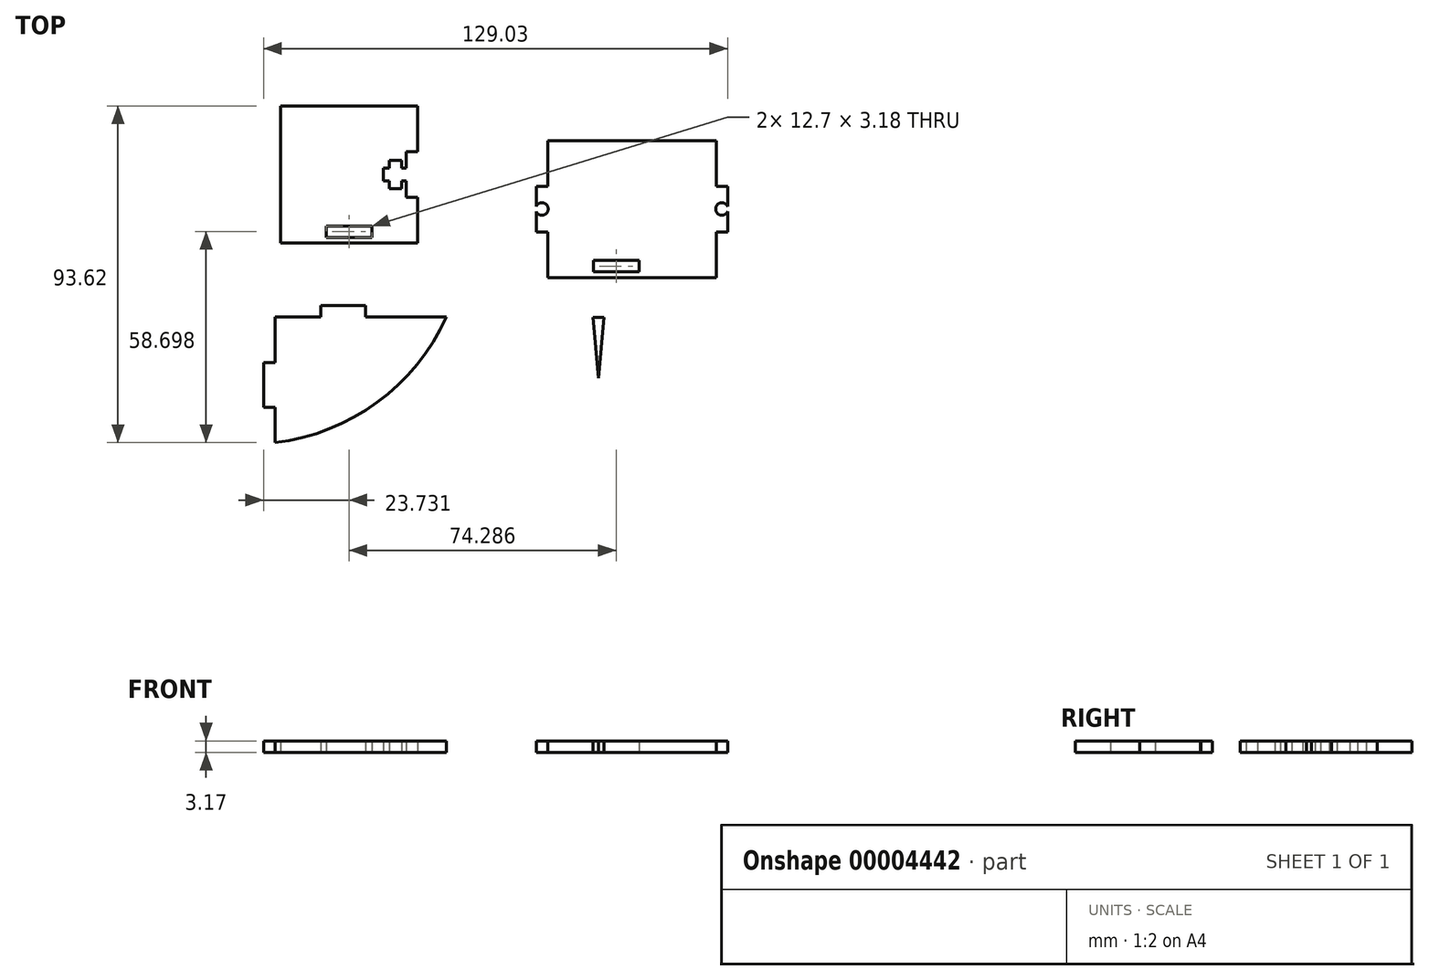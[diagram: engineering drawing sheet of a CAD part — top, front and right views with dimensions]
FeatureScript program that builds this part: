
annotation { "Feature Type Name" : "Feature", "Feature Type Description" : "" }
export const myFeature = defineFeature(function(context is Context, id is Id, definition is map)
    precondition{}
    {
        {
            var Q0;
            Q0=qCreatedBy(makeId("Top.planeOp"),FACE);
            var sketch = newSketch(context, id + "F0", { "sketchPlane" : qUnion([Q0])});
            skLineSegment(sketch, "E0.bottom", {"start": v(-61.4, 49.08) * mm, "end": v(-23.3, 49.08) * mm});
            skLineSegment(sketch, "E0.top", {"start": v(-61.4, 10.98) * mm, "end": v(-23.3, 10.98) * mm});
            skLineSegment(sketch, "E0.left", {"start": v(-61.4, 49.08) * mm, "end": v(-61.4, 10.98) * mm});
            skLineSegment(sketch, "E0.right", {"start": v(-23.3, 49.08) * mm, "end": v(-23.3, 10.98) * mm});
            skLineSegment(sketch, "E1.bottom", {"start": v(-48.7, 15.75) * mm, "end": v(-36, 15.75) * mm});
            skLineSegment(sketch, "E1.top", {"start": v(-48.7, 12.57) * mm, "end": v(-36, 12.57) * mm});
            skLineSegment(sketch, "E1.left", {"start": v(-48.7, 15.75) * mm, "end": v(-48.7, 12.57) * mm});
            skLineSegment(sketch, "E1.right", {"start": v(-36, 15.75) * mm, "end": v(-36, 12.57) * mm});
            skLineSegment(sketch, "E2.bottom", {"start": v(-23.3, 36.38) * mm, "end": v(-26.48, 36.38) * mm});
            skLineSegment(sketch, "E2.top", {"start": v(-23.3, 23.68) * mm, "end": v(-26.48, 23.68) * mm});
            skLineSegment(sketch, "E2.left", {"start": v(-23.3, 36.38) * mm, "end": v(-23.3, 23.68) * mm});
            skLineSegment(sketch, "E2.right", {"start": v(-26.48, 36.38) * mm, "end": v(-26.48, 23.68) * mm});
            skLineSegment(sketch, "E3.bottom", {"start": v(-23.3, 31.79) * mm, "end": v(-32.83, 31.79) * mm});
            skLineSegment(sketch, "E3.top", {"start": v(-23.3, 28.28) * mm, "end": v(-32.83, 28.28) * mm});
            skLineSegment(sketch, "E3.left", {"start": v(-23.3, 31.79) * mm, "end": v(-23.3, 28.28) * mm});
            skLineSegment(sketch, "E3.right", {"start": v(-32.83, 31.79) * mm, "end": v(-32.83, 28.28) * mm});
            skLineSegment(sketch, "E4.bottom", {"start": v(-31.1, 34) * mm, "end": v(-27.75, 34) * mm});
            skLineSegment(sketch, "E4.top", {"start": v(-31.1, 26.06) * mm, "end": v(-27.75, 26.06) * mm});
            skLineSegment(sketch, "E4.left", {"start": v(-31.1, 34) * mm, "end": v(-31.1, 26.06) * mm});
            skLineSegment(sketch, "E4.right", {"start": v(-27.75, 34) * mm, "end": v(-27.75, 26.06) * mm});
            skSolve(sketch);
        }
        {
            var Q0;
            Q0=qCreatedBy(makeId("Top.planeOp"),FACE);
            var sketch = newSketch(context, id + "F1", { "sketchPlane" : qUnion([Q0])});
            skLineSegment(sketch, "E5.bottom", {"start": v(12.88, 39.5) * mm, "end": v(59.77, 39.5) * mm});
            skLineSegment(sketch, "E5.top", {"start": v(12.88, 1.4) * mm, "end": v(59.77, 1.4) * mm});
            skLineSegment(sketch, "E5.left", {"start": v(12.88, 39.5) * mm, "end": v(12.88, 1.4) * mm});
            skLineSegment(sketch, "E5.right", {"start": v(59.77, 39.5) * mm, "end": v(59.77, 1.4) * mm});
            skLineSegment(sketch, "E6.bottom", {"start": v(25.58, 6.16) * mm, "end": v(38.28, 6.16) * mm});
            skLineSegment(sketch, "E6.top", {"start": v(25.58, 2.98) * mm, "end": v(38.28, 2.98) * mm});
            skLineSegment(sketch, "E6.left", {"start": v(25.58, 6.16) * mm, "end": v(25.58, 2.98) * mm});
            skLineSegment(sketch, "E6.right", {"start": v(38.28, 6.16) * mm, "end": v(38.28, 2.98) * mm});
            skLineSegment(sketch, "E7.bottom", {"start": v(59.77, 26.8) * mm, "end": v(62.94, 26.8) * mm});
            skLineSegment(sketch, "E7.top", {"start": v(59.77, 14.1) * mm, "end": v(62.94, 14.1) * mm});
            skLineSegment(sketch, "E7.left", {"start": v(59.77, 26.8) * mm, "end": v(59.77, 14.1) * mm});
            skLineSegment(sketch, "E7.right", {"start": v(62.94, 26.8) * mm, "end": v(62.94, 14.1) * mm});
            skLineSegment(sketch, "E8.bottom", {"start": v(12.88, 26.8) * mm, "end": v(9.7, 26.8) * mm});
            skLineSegment(sketch, "E8.top", {"start": v(12.88, 14.1) * mm, "end": v(9.7, 14.1) * mm});
            skLineSegment(sketch, "E8.left", {"start": v(12.88, 26.8) * mm, "end": v(12.88, 14.1) * mm});
            skLineSegment(sketch, "E8.right", {"start": v(9.7, 26.8) * mm, "end": v(9.7, 14.1) * mm});
            skCircle(sketch, "E9", {"center": v(61.35, 20.45) * mm, "radius": 1.75 * mm});
            skCircle(sketch, "E10", {"center": v(11.29, 20.45) * mm, "radius": 1.75 * mm});
            skSolve(sketch);
        }
        {
            var Q0;
            Q0=qCreatedBy(makeId("Top.planeOp"),FACE);
            var sketch = newSketch(context, id + "F2", { "sketchPlane" : qUnion([Q0])});
            skLineSegment(sketch, "E11", {"start": v(-62.92, -44.54) * mm, "end": v(-62.92, -34.76) * mm});
            skLineSegment(sketch, "E12", {"start": v(-62.92, -9.61) * mm, "end": v(-50.22, -9.61) * mm});
            skLineSegment(sketch, "E13.bottom", {"start": v(-50.22, -6.44) * mm, "end": v(-37.77, -6.44) * mm});
            skLineSegment(sketch, "E13.left", {"start": v(-50.22, -6.44) * mm, "end": v(-50.22, -9.61) * mm});
            skLineSegment(sketch, "E13.right", {"start": v(-37.77, -6.44) * mm, "end": v(-37.77, -9.61) * mm});
            skLineSegment(sketch, "E14.bottom", {"start": v(-62.92, -22.31) * mm, "end": v(-66.1, -22.31) * mm});
            skLineSegment(sketch, "E14.top", {"start": v(-62.92, -34.76) * mm, "end": v(-66.1, -34.76) * mm});
            skLineSegment(sketch, "E14.right", {"start": v(-66.1, -22.31) * mm, "end": v(-66.1, -34.76) * mm});
            skLineSegment(sketch, "E15.trimOffspring", {"start": v(-62.92, -22.31) * mm, "end": v(-62.92, -9.61) * mm});
            skLineSegment(sketch, "E16.trimOffspring", {"start": v(-37.77, -9.61) * mm, "end": v(-15.3, -9.61) * mm});
            skArc(sketch, "E17", {"start": v(-62.92, -44.54) * mm, "mid": v(-34.5, -33.34) * mm, "end": v(-15.3, -9.61) * mm});
            skSolve(sketch);
        }
        {
            var Q0;
            Q0=qCreatedBy(makeId("Top.planeOp"),FACE);
            var sketch = newSketch(context, id + "F3", { "sketchPlane" : qUnion([Q0])});
            skLineSegment(sketch, "E18.bottom", {"start": v(8.46, -9.7) * mm, "end": v(27.4, -9.7) * mm});
            skLineSegment(sketch, "E18.top", {"start": v(8.46, -47.8) * mm, "end": v(27.4, -47.8) * mm});
            skLineSegment(sketch, "E18.left", {"start": v(8.46, -9.7) * mm, "end": v(8.46, -47.8) * mm});
            skLineSegment(sketch, "E19", {"start": v(22.44, -28.76) * mm, "end": v(23.96, -12.28) * mm});
            skLineSegment(sketch, "E20", {"start": v(23.96, -12.28) * mm, "end": v(25.49, -28.76) * mm});
            skLineSegment(sketch, "E21", {"start": v(25.49, -9.7) * mm, "end": v(27, -26.56) * mm});
            skLineSegment(sketch, "E22.0.MirrorCS", {"start": v(22.44, -28.76) * mm, "end": v(23.96, -45.24) * mm});
            skLineSegment(sketch, "E23.0.MirrorCS", {"start": v(23.96, -45.24) * mm, "end": v(25.49, -28.76) * mm});
            skLineSegment(sketch, "E24.0.MirrorCS", {"start": v(25.12, -47.8) * mm, "end": v(26.64, -30.96) * mm});
            skLineSegment(sketch, "E25.0.MirrorCS", {"start": v(28.53, -9.7) * mm, "end": v(27, -26.56) * mm});
            skLineSegment(sketch, "E26.0.MirrorCS", {"start": v(30.06, -12.28) * mm, "end": v(28.53, -28.76) * mm});
            skLineSegment(sketch, "E27.0.MirrorCS", {"start": v(31.58, -28.76) * mm, "end": v(30.06, -12.28) * mm});
            skLineSegment(sketch, "E28.0.MirrorCS", {"start": v(31.58, -28.76) * mm, "end": v(30.06, -45.24) * mm});
            skLineSegment(sketch, "E29.0.MirrorCS", {"start": v(30.06, -45.24) * mm, "end": v(28.53, -28.76) * mm});
            skLineSegment(sketch, "E30.0.MirrorCS", {"start": v(28.17, -47.8) * mm, "end": v(26.64, -30.96) * mm});
            skLineSegment(sketch, "E31.0.MirrorCS", {"start": v(31.58, -47.8) * mm, "end": v(33.1, -30.96) * mm});
            skLineSegment(sketch, "E32.0.MirrorCS", {"start": v(34.63, -47.8) * mm, "end": v(33.1, -30.96) * mm});
            skLineSegment(sketch, "E33.0.MirrorCS", {"start": v(31.58, -9.7) * mm, "end": v(33.1, -26.56) * mm});
            skLineSegment(sketch, "E34.0.MirrorCS", {"start": v(34.63, -9.7) * mm, "end": v(33.1, -26.56) * mm});
            skLineSegment(sketch, "E35.0.MirrorCS", {"start": v(36.15, -45.24) * mm, "end": v(34.63, -28.76) * mm});
            skLineSegment(sketch, "E36.0.MirrorCS", {"start": v(37.68, -28.76) * mm, "end": v(36.15, -45.24) * mm});
            skLineSegment(sketch, "E37.0.MirrorCS", {"start": v(37.68, -28.76) * mm, "end": v(36.15, -12.28) * mm});
            skLineSegment(sketch, "E38.0.MirrorCS", {"start": v(36.15, -12.28) * mm, "end": v(34.63, -28.76) * mm});
            skLineSegment(sketch, "E39.0.MirrorCS", {"start": v(37.68, -47.8) * mm, "end": v(39.2, -30.96) * mm});
            skLineSegment(sketch, "E40.0.MirrorCS", {"start": v(40.73, -47.8) * mm, "end": v(39.2, -30.96) * mm});
            skLineSegment(sketch, "E41.0.MirrorCS", {"start": v(37.68, -9.7) * mm, "end": v(39.2, -26.56) * mm});
            skLineSegment(sketch, "E42.0.MirrorCS", {"start": v(40.73, -9.7) * mm, "end": v(39.2, -26.56) * mm});
            skLineSegment(sketch, "E43.0.MirrorCS", {"start": v(40.73, -28.76) * mm, "end": v(42.25, -12.28) * mm});
            skLineSegment(sketch, "E44.0.MirrorCS", {"start": v(42.25, -12.28) * mm, "end": v(43.77, -28.76) * mm});
            skLineSegment(sketch, "E45.0.MirrorCS", {"start": v(43.77, -9.7) * mm, "end": v(45.3, -26.56) * mm});
            skLineSegment(sketch, "E46.0.MirrorCS", {"start": v(46.82, -9.7) * mm, "end": v(45.3, -26.56) * mm});
            skLineSegment(sketch, "E47.0.MirrorCS", {"start": v(48.35, -12.28) * mm, "end": v(46.82, -28.76) * mm});
            skLineSegment(sketch, "E48.0.MirrorCS", {"start": v(49.87, -28.76) * mm, "end": v(48.35, -12.28) * mm});
            skLineSegment(sketch, "E49.0.MirrorCS", {"start": v(49.87, -28.76) * mm, "end": v(48.35, -45.24) * mm});
            skLineSegment(sketch, "E50.0.MirrorCS", {"start": v(48.35, -45.24) * mm, "end": v(46.82, -28.76) * mm});
            skLineSegment(sketch, "E51.0.MirrorCS", {"start": v(46.82, -47.8) * mm, "end": v(45.3, -30.96) * mm});
            skLineSegment(sketch, "E52.0.MirrorCS", {"start": v(43.77, -47.8) * mm, "end": v(45.3, -30.96) * mm});
            skLineSegment(sketch, "E53.0.MirrorCS", {"start": v(42.25, -45.24) * mm, "end": v(43.77, -28.76) * mm});
            skLineSegment(sketch, "E54.0.MirrorCS", {"start": v(40.73, -28.76) * mm, "end": v(42.25, -45.24) * mm});
            skLineSegment(sketch, "E55", {"start": v(25.49, -9.7) * mm, "end": v(65.47, -9.7) * mm});
            skLineSegment(sketch, "E56", {"start": v(27.4, -47.8) * mm, "end": v(65.47, -47.8) * mm});
            skLineSegment(sketch, "E57.0.MirrorCS", {"start": v(49.87, -9.7) * mm, "end": v(51.4, -26.56) * mm});
            skLineSegment(sketch, "E58.0.MirrorCS", {"start": v(52.92, -9.7) * mm, "end": v(51.4, -26.56) * mm});
            skLineSegment(sketch, "E59.0.MirrorCS", {"start": v(54.44, -12.28) * mm, "end": v(52.92, -28.76) * mm});
            skLineSegment(sketch, "E60.0.MirrorCS", {"start": v(55.97, -28.76) * mm, "end": v(54.44, -12.28) * mm});
            skLineSegment(sketch, "E61.0.MirrorCS", {"start": v(55.97, -9.7) * mm, "end": v(57.49, -26.56) * mm});
            skLineSegment(sketch, "E62.0.MirrorCS", {"start": v(59.01, -9.7) * mm, "end": v(57.49, -26.56) * mm});
            skLineSegment(sketch, "E63.0.MirrorCS", {"start": v(59.01, -28.76) * mm, "end": v(60.54, -12.28) * mm});
            skLineSegment(sketch, "E64.0.MirrorCS", {"start": v(60.54, -12.28) * mm, "end": v(62.06, -28.76) * mm});
            skLineSegment(sketch, "E65.0.MirrorCS", {"start": v(62.06, -9.7) * mm, "end": v(63.59, -26.56) * mm});
            skLineSegment(sketch, "E66.0.MirrorCS", {"start": v(65.1, -9.7) * mm, "end": v(63.59, -26.56) * mm});
            skLineSegment(sketch, "E67.0.MirrorCS", {"start": v(65.1, -47.8) * mm, "end": v(63.59, -30.96) * mm});
            skLineSegment(sketch, "E68.0.MirrorCS", {"start": v(62.06, -47.8) * mm, "end": v(63.59, -30.96) * mm});
            skLineSegment(sketch, "E69.0.MirrorCS", {"start": v(60.54, -45.24) * mm, "end": v(62.06, -28.76) * mm});
            skLineSegment(sketch, "E70.0.MirrorCS", {"start": v(59.01, -28.76) * mm, "end": v(60.54, -45.24) * mm});
            skLineSegment(sketch, "E71.0.MirrorCS", {"start": v(59.01, -47.8) * mm, "end": v(57.49, -30.96) * mm});
            skLineSegment(sketch, "E72.0.MirrorCS", {"start": v(55.97, -47.8) * mm, "end": v(57.49, -30.96) * mm});
            skLineSegment(sketch, "E73.0.MirrorCS", {"start": v(55.97, -28.76) * mm, "end": v(54.44, -45.24) * mm});
            skLineSegment(sketch, "E74.0.MirrorCS", {"start": v(54.44, -45.24) * mm, "end": v(52.92, -28.76) * mm});
            skLineSegment(sketch, "E75.0.MirrorCS", {"start": v(52.92, -47.8) * mm, "end": v(51.4, -30.96) * mm});
            skLineSegment(sketch, "E76.0.MirrorCS", {"start": v(49.87, -47.8) * mm, "end": v(51.4, -30.96) * mm});
            skLineSegment(sketch, "E77.bottom", {"start": v(65.47, -9.7) * mm, "end": v(71.65, -9.7) * mm});
            skLineSegment(sketch, "E77.top", {"start": v(65.47, -47.8) * mm, "end": v(71.65, -47.8) * mm});
            skLineSegment(sketch, "E77.right", {"start": v(71.65, -9.7) * mm, "end": v(71.65, -47.8) * mm});
            skLineSegment(sketch, "E78.bottom", {"start": v(8.46, -22.4) * mm, "end": v(11.63, -22.4) * mm});
            skLineSegment(sketch, "E78.top", {"start": v(8.46, -35.1) * mm, "end": v(11.63, -35.1) * mm});
            skLineSegment(sketch, "E78.left", {"start": v(8.46, -22.4) * mm, "end": v(8.46, -35.1) * mm});
            skLineSegment(sketch, "E78.right", {"start": v(11.63, -22.4) * mm, "end": v(11.63, -35.1) * mm});
            skLineSegment(sketch, "E79.bottom", {"start": v(8.46, -27) * mm, "end": v(17.98, -27) * mm});
            skLineSegment(sketch, "E79.top", {"start": v(8.46, -30.51) * mm, "end": v(17.98, -30.51) * mm});
            skLineSegment(sketch, "E79.left", {"start": v(8.46, -27) * mm, "end": v(8.46, -30.51) * mm});
            skLineSegment(sketch, "E79.right", {"start": v(17.98, -27) * mm, "end": v(17.98, -30.51) * mm});
            skLineSegment(sketch, "E80.bottom", {"start": v(12.9, -24.78) * mm, "end": v(16.25, -24.78) * mm});
            skLineSegment(sketch, "E80.top", {"start": v(12.9, -32.73) * mm, "end": v(16.25, -32.73) * mm});
            skLineSegment(sketch, "E80.left", {"start": v(12.9, -24.78) * mm, "end": v(12.9, -32.73) * mm});
            skLineSegment(sketch, "E80.right", {"start": v(16.25, -24.78) * mm, "end": v(16.25, -32.73) * mm});
            skSolve(sketch);
        }
        {
            var Q0;
            {var subQ4=sQuery(id+"F0.wireOp",EDGE,"E0.bottom");Q0=makeQuery(id+"F0.imprint","IMPRINT",FACE,{"disambiguationData":[TD([[makeQuery(id+"F0.imprint","IMPRINT",EDGE,{"derivedFrom":subQ4}),-1.0]])]});}
            extrude(context, id + "F4", {"entities" : qUnion([Q0]), "depth" : 3.17 * mm});
        }
        {
            var Q0;
            {var subQ5=sQuery(id+"F1.wireOp",EDGE,"E7.bottom");Q0=makeQuery(id+"F1.imprint","IMPRINT",FACE,{"disambiguationData":[TD([[makeQuery(id+"F1.imprint","IMPRINT",EDGE,{"derivedFrom":subQ5}),-1.0]])]});}
            var Q1;
            {var subQ5=sQuery(id+"F1.wireOp",EDGE,"E7.top");Q1=makeQuery(id+"F1.imprint","IMPRINT",FACE,{"disambiguationData":[TD([[makeQuery(id+"F1.imprint","IMPRINT",EDGE,{"derivedFrom":subQ5}),1.0]])]});}
            var Q2;
            {var subQ5=sQuery(id+"F1.wireOp",EDGE,"E8.bottom");Q2=makeQuery(id+"F1.imprint","IMPRINT",FACE,{"disambiguationData":[TD([[makeQuery(id+"F1.imprint","IMPRINT",EDGE,{"derivedFrom":subQ5}),1.0]])]});}
            var Q3;
            {var subQ5=sQuery(id+"F1.wireOp",EDGE,"E8.top");Q3=makeQuery(id+"F1.imprint","IMPRINT",FACE,{"disambiguationData":[TD([[makeQuery(id+"F1.imprint","IMPRINT",EDGE,{"derivedFrom":subQ5}),-1.0]])]});}
            var Q4;
            {var subQ15=sQuery(id+"F1.wireOp",EDGE,"E5.bottom");Q4=makeQuery(id+"F1.imprint","IMPRINT",FACE,{"disambiguationData":[TD([[makeQuery(id+"F1.imprint","IMPRINT",EDGE,{"derivedFrom":subQ15}),-1.0]])]});}
            extrude(context, id + "F5", {"entities" : qUnion([Q0, Q1, Q2, Q3, Q4]), "depth" : 3.17 * mm});
        }
        {
            var Q0;
            Q0=makeQuery(id+"F2.imprint","IMPRINT",FACE,{"disambiguationData":[TD([[makeQuery(id+"F2.imprint","IMPRINT",EDGE,{"derivedFrom":sQuery(id+"F2.wireOp",EDGE,"E11")}),-1.0]])]});
            extrude(context, id + "F6", {"entities" : qUnion([Q0]), "depth" : 3.17 * mm});
        }
        {
            var Q0;
            {var subQ28=sQuery(id+"F3.wireOp",EDGE,"E18.bottom");Q0=makeQuery(id+"F3.imprint","IMPRINT",FACE,{"disambiguationData":[TD([[makeQuery(id+"F3.imprint","IMPRINT",EDGE,{"derivedFrom":subQ28}),-1.0]])]});}
            extrude(context, id + "F7", {"entities" : qUnion([Q0]), "depth" : 3.17 * mm});
        }
    });
